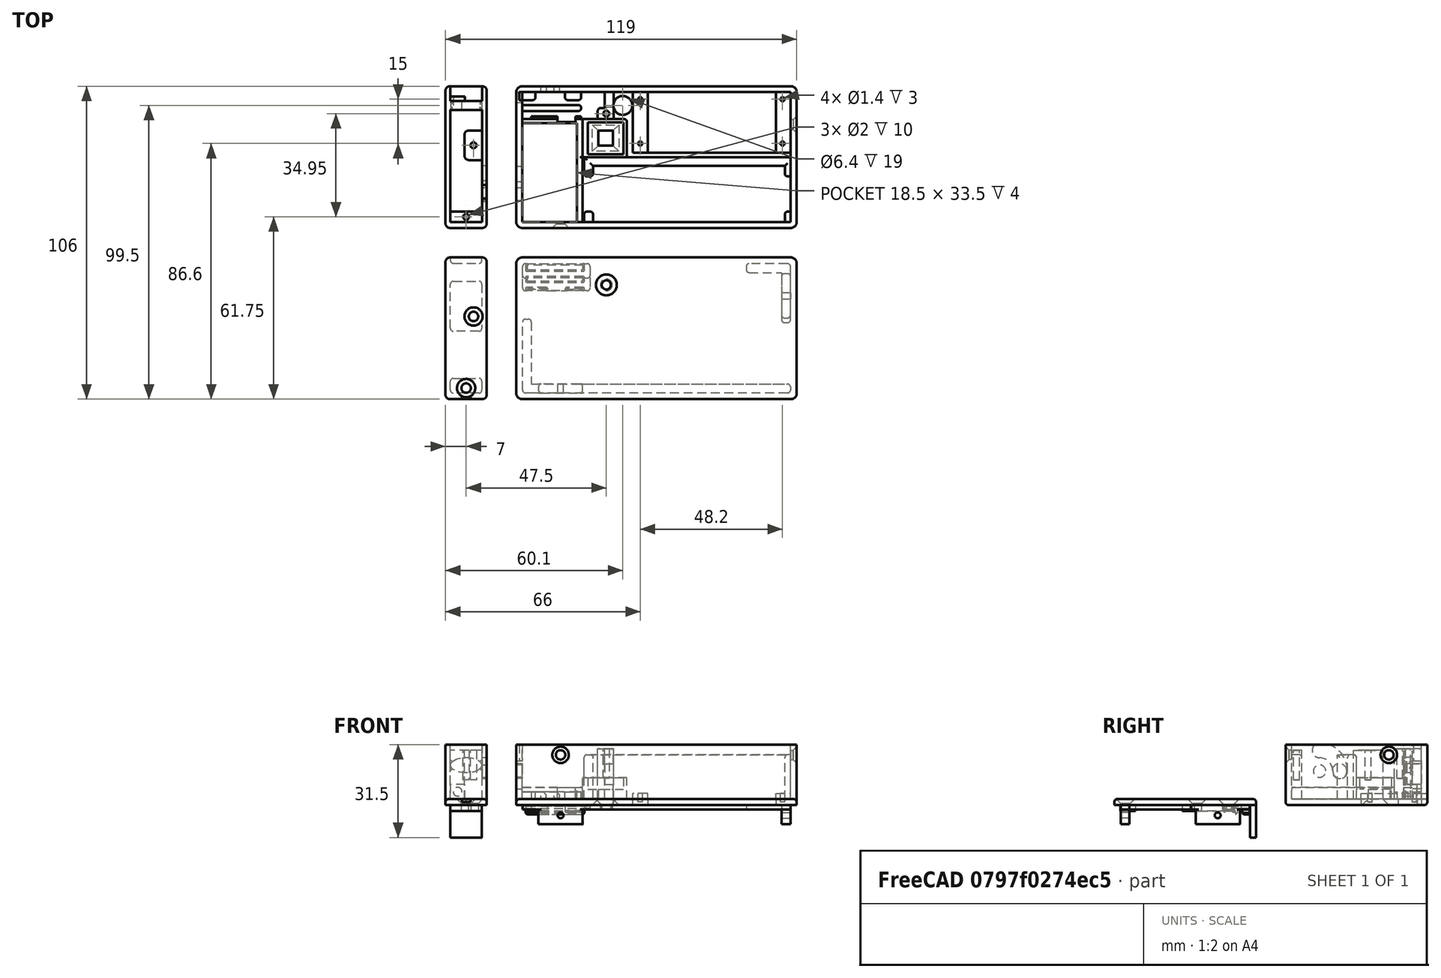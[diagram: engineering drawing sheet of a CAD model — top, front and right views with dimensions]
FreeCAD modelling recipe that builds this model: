
FCSTD DOCUMENT  (FreeCAD 0.19R23756 (Git))
Label: uv_case
License: All rights reserved
LicenseURL: http://en.wikipedia.org/wiki/All_rights_reserved
objects: Sketcher::SketchObject×52, PartDesign::Pocket×23, PartDesign::Pad×22, PartDesign::Fillet×16, PartDesign::Chamfer×7, PartDesign::Body×4, Mesh::Feature×4
note: 192 computed .brp shape members not serialized (recipe doc carries the construction recipe); baked Part::Feature solids carry a one-line shape summary decoded from their .brp

FEATURE [Sketcher::SketchObject] Sketch
  FullyConstrained = true
  MapMode = 5
  Support = -> [XY_Plane]
  sketch-geometry (4):
    g0: LineSegment StartX=0 StartY=0 StartZ=0 EndX=95 EndY=0 EndZ=0
    g1: LineSegment StartX=95 StartY=0 StartZ=0 EndX=95 EndY=48 EndZ=0
    g2: LineSegment StartX=95 StartY=48 StartZ=0 EndX=0 EndY=48 EndZ=0
    g3: LineSegment StartX=0 StartY=48 StartZ=0 EndX=0 EndY=0 EndZ=0
  constraints (11):
    c: Coincident(g0,g1)
    c: Coincident(g1,g2)
    c: Coincident(g2,g3)
    c: Coincident(g3,g0)
    c: Horizontal(g0)
    c: Horizontal(g2)
    c: Vertical(g1)
    c: Vertical(g3)
    c: Coincident(g0,g-1)
    c: DistanceX(g2,g2) = 95
    c: DistanceY(g3,g3) = 48
FEATURE [PartDesign::Pad] Pad
  Direction = (1,1,1)
  Length = 2
  Length2 = 100
  Profile = -> Sketch
  Type = 0
FEATURE [Sketcher::SketchObject] Sketch001
  ExternalGeometry = -> [Pad]
  FullyConstrained = true
  MapMode = 5
  Placement = pos=(0,0,2) rot=(0,0,1;0rad)
  Support = -> [Pad]
  sketch-geometry (8):
    g0: LineSegment StartX=0 StartY=0 StartZ=0 EndX=95 EndY=0 EndZ=0
    g1: LineSegment StartX=95 StartY=0 StartZ=0 EndX=95 EndY=48 EndZ=0
    g2: LineSegment StartX=95 StartY=48 StartZ=0 EndX=0 EndY=48 EndZ=0
    g3: LineSegment StartX=0 StartY=48 StartZ=0 EndX=0 EndY=0 EndZ=0
    g4: LineSegment StartX=2 StartY=2 StartZ=0 EndX=93 EndY=2 EndZ=0
    g5: LineSegment StartX=93 StartY=2 StartZ=0 EndX=93 EndY=46 EndZ=0
    g6: LineSegment StartX=93 StartY=46 StartZ=0 EndX=2 EndY=46 EndZ=0
    g7: LineSegment StartX=2 StartY=46 StartZ=0 EndX=2 EndY=2 EndZ=0
  constraints (22):
    c: Coincident(g0,g1)
    c: Coincident(g1,g2)
    c: Coincident(g2,g3)
    c: Coincident(g3,g0)
    c: Horizontal(g0)
    c: Horizontal(g2)
    c: Vertical(g1)
    c: Vertical(g3)
    c: Coincident(g0,g-1)
    c: Coincident(g1,g-3)
    c: Coincident(g4,g5)
    c: Coincident(g5,g6)
    c: Coincident(g6,g7)
    c: Coincident(g7,g4)
    c: Horizontal(g4)
    c: Horizontal(g6)
    c: Vertical(g5)
    c: Vertical(g7)
    c: DistanceX(g5,g1) = 2
    c: DistanceY(g5,g1) = 2
    c: DistanceX(g0,g4) = 2
    c: DistanceY(g0,g4) = 2
FEATURE [PartDesign::Pad] Pad001
  BaseFeature = -> Pad
  Direction = (1,1,1)
  Length = 18.5
  Length2 = 100
  Profile = -> Sketch001
  Type = 0
FEATURE [Sketcher::SketchObject] Sketch002
  ExternalGeometry = -> [Pad001]
  FullyConstrained = true
  MapMode = 5
  Placement = pos=(0,0,2) rot=(0,0,1;0rad)
  Support = -> [Pad001]
  sketch-geometry (4):
    g0: LineSegment StartX=44.5 StartY=46 StartZ=0 EndX=88 EndY=46 EndZ=0
    g1: LineSegment StartX=88 StartY=46 StartZ=0 EndX=88 EndY=25.5 EndZ=0
    g2: LineSegment StartX=88 StartY=25.5 StartZ=0 EndX=44.5 EndY=25.5 EndZ=0
    g3: LineSegment StartX=44.5 StartY=25.5 StartZ=0 EndX=44.5 EndY=46 EndZ=0
  constraints (12):
    c: Coincident(g0,g1)
    c: Coincident(g1,g2)
    c: Coincident(g2,g3)
    c: Coincident(g3,g0)
    c: Horizontal(g0)
    c: Horizontal(g2)
    c: Vertical(g1)
    c: Vertical(g3)
    c: Horizontal(g0,g-3)
    c: DistanceX(g0,g-3) = 5
    c: DistanceX(g2,g2) = 43.5
    c: DistanceY(g3,g3) = 20.5
FEATURE [PartDesign::Pocket] Pocket
  BaseFeature = -> Pad001
  Length = 5
  Length2 = 100
  Profile = -> Sketch002
  Type = 0
FEATURE [Sketcher::SketchObject] Sketch003
  ExternalGeometry = -> [Pocket]
  FullyConstrained = true
  MapMode = 5
  Placement = pos=(0,0,2) rot=(0,0,1;0rad)
  Support = -> [Pocket]
  sketch-geometry (8):
    g0: LineSegment StartX=39.5 StartY=25.5 StartZ=0 EndX=44.5 EndY=25.5 EndZ=0
    g1: LineSegment StartX=44.5 StartY=25.5 StartZ=0 EndX=44.5 EndY=46 EndZ=0
    g2: LineSegment StartX=44.5 StartY=46 StartZ=0 EndX=39.5 EndY=46 EndZ=0
    g3: LineSegment StartX=39.5 StartY=46 StartZ=0 EndX=39.5 EndY=25.5 EndZ=0
    g4: LineSegment StartX=88 StartY=46 StartZ=0 EndX=93 EndY=46 EndZ=0
    g5: LineSegment StartX=93 StartY=46 StartZ=0 EndX=93 EndY=25.5 EndZ=0
    g6: LineSegment StartX=93 StartY=25.5 StartZ=0 EndX=88 EndY=25.5 EndZ=0
    g7: LineSegment StartX=88 StartY=25.5 StartZ=0 EndX=88 EndY=46 EndZ=0
  constraints (20):
    c: Coincident(g0,g1)
    c: Coincident(g1,g2)
    c: Coincident(g2,g3)
    c: Coincident(g3,g0)
    c: Horizontal(g0)
    c: Horizontal(g2)
    c: Vertical(g3)
    c: Coincident(g4,g5)
    c: Coincident(g5,g6)
    c: Coincident(g6,g7)
    c: Coincident(g7,g4)
    c: Horizontal(g4)
    c: Horizontal(g6)
    c: Vertical(g5)
    c: Coincident(g1,g-4)
    c: Coincident(g0,g-4)
    c: Coincident(g6,g-3)
    c: Coincident(g4,g-3)
    c: DistanceX(g6,g6) = 5
    c: DistanceX(g0,g0) = 5
FEATURE [PartDesign::Pad] Pad002
  BaseFeature = -> Pocket
  Direction = (1,1,1)
  Length = 2
  Length2 = 100
  Profile = -> Sketch003
  Type = 0
FEATURE [Sketcher::SketchObject] Sketch004
  ExternalGeometry = -> [Pad002]
  FullyConstrained = true
  MapMode = 5
  Placement = pos=(0,0,4) rot=(0,0,1;0rad)
  Support = -> [Pad002]
  sketch-geometry (4):
    g0: Circle CenterX=90.2 CenterY=43.6 CenterZ=0 NormalX=0 NormalY=0 NormalZ=1 AngleXU=0 Radius=0.7
    g1: Circle CenterX=90.2 CenterY=28.6 CenterZ=0 NormalX=0 NormalY=0 NormalZ=1 AngleXU=0 Radius=0.7
    g2: Circle CenterX=42 CenterY=43.6 CenterZ=0 NormalX=0 NormalY=0 NormalZ=1 AngleXU=0 Radius=0.7
    g3: Circle CenterX=42 CenterY=28.6 CenterZ=0 NormalX=0 NormalY=0 NormalZ=1 AngleXU=0 Radius=0.7
  constraints (12):
    c: DistanceX(g-3,g0) = 2.2
    c: DistanceX(g2,g-4) = 2.5
    c: Vertical(g2,g3)
    c: Vertical(g0,g1)
    c: Horizontal(g1,g3)
    c: Horizontal(g2,g0)
    c: Equal(g0,g2)
    c: Equal(g2,g3)
    c: Equal(g3,g1)
    c: DistanceY(g3,g2) = 15
    c: DistanceY(g2,g-4) = 2.4
    c: Radius(g2) = 0.7
FEATURE [PartDesign::Pocket] Pocket001
  BaseFeature = -> Pad002
  Length = 3
  Length2 = 100
  Profile = -> Sketch004
  Type = 0
FEATURE [Sketcher::SketchObject] Sketch005
  ExternalGeometry = -> [Pocket001]
  FullyConstrained = true
  MapMode = 5
  Placement = pos=(0,0,2) rot=(0,0,1;0rad)
  Support = -> [Pocket001]
  sketch-geometry (20):
    g0: LineSegment StartX=2 StartY=46 StartZ=0 EndX=6.5 EndY=46 EndZ=0
    g1: LineSegment StartX=6.5 StartY=46 StartZ=0 EndX=6.5 EndY=43.3 EndZ=0
    g2: LineSegment StartX=6.5 StartY=43.3 StartZ=0 EndX=2 EndY=43.3 EndZ=0
    g3: LineSegment StartX=2 StartY=43.3 StartZ=0 EndX=2 EndY=46 EndZ=0
    g4: LineSegment StartX=16.5 StartY=46 StartZ=0 EndX=22 EndY=46 EndZ=0
    g5: LineSegment StartX=22 StartY=46 StartZ=0 EndX=22 EndY=43.3 EndZ=0
    g6: LineSegment StartX=22 StartY=43.3 StartZ=0 EndX=16.5 EndY=43.3 EndZ=0
    g7: LineSegment StartX=16.5 StartY=43.3 StartZ=0 EndX=16.5 EndY=46 EndZ=0
    g8: LineSegment StartX=2 StartY=41.6 StartZ=0 EndX=22 EndY=41.6 EndZ=0
    g9: LineSegment StartX=22 StartY=41.6 StartZ=0 EndX=22 EndY=39.6 EndZ=0
    g10: LineSegment StartX=22 StartY=39.6 StartZ=0 EndX=2 EndY=39.6 EndZ=0
    g11: LineSegment StartX=2 StartY=39.6 StartZ=0 EndX=2 EndY=41.6 EndZ=0
    g12: LineSegment StartX=2 StartY=36.85 StartZ=0 EndX=14 EndY=36.85 EndZ=0
    g13: LineSegment StartX=14 StartY=36.85 StartZ=0 EndX=14 EndY=37.85 EndZ=0
    g14: LineSegment StartX=14 StartY=37.85 StartZ=0 EndX=2 EndY=37.85 EndZ=0
    g15: LineSegment StartX=2 StartY=37.85 StartZ=0 EndX=2 EndY=36.85 EndZ=0
    g16: LineSegment StartX=20 StartY=37.85 StartZ=0 EndX=22 EndY=37.85 EndZ=0
    g17: LineSegment StartX=22 StartY=37.85 StartZ=0 EndX=22 EndY=36.85 EndZ=0
    g18: LineSegment StartX=22 StartY=36.85 StartZ=0 EndX=20 EndY=36.85 EndZ=0
    g19: LineSegment StartX=20 StartY=36.85 StartZ=0 EndX=20 EndY=37.85 EndZ=0
  constraints (59):
    c: Coincident(g0,g1)
    c: Coincident(g1,g2)
    c: Coincident(g2,g3)
    c: Coincident(g3,g0)
    c: Horizontal(g0)
    c: Horizontal(g2)
    c: Vertical(g1)
    c: Vertical(g3)
    c: Coincident(g4,g5)
    c: Coincident(g5,g6)
    c: Coincident(g6,g7)
    c: Coincident(g7,g4)
    c: Horizontal(g4)
    c: Horizontal(g6)
    c: Vertical(g5)
    c: Vertical(g7)
    c: Coincident(g8,g9)
    c: Coincident(g9,g10)
    c: Coincident(g10,g11)
    c: Coincident(g11,g8)
    c: Horizontal(g8)
    c: Vertical(g9)
    c: Vertical(g11)
    c: Coincident(g12,g13)
    c: Coincident(g13,g14)
    c: Coincident(g14,g15)
    c: Coincident(g15,g12)
    c: Horizontal(g12)
    c: Horizontal(g14)
    c: Vertical(g13)
    c: Vertical(g15)
    c: DistanceY(g3,g3) = 2.7
    c: DistanceX(g0,g0) = 4.5
    c: Coincident(g0,g-3)
    c: Horizontal(g4,g0)
    c: Horizontal(g6,g1)
    c: DistanceX(g0,g4) = 14.5
    c: DistanceX(g0,g4) = 20
    c: DistanceY(g8,g2) = 1.7
    c: DistanceX(g8,g8) = 20
    c: DistanceY(g11,g11) = 2
    c: Vertical(g8,g2)
    c: Horizontal(g10)
    c: DistanceX(g14,g14) = 12
    c: DistanceY(g15,g15) = 1
    c: Vertical(g14,g10)
    c: DistanceY(g14,g10) = 1.75
    c: Coincident(g16,g17)
    c: Coincident(g17,g18)
    c: Coincident(g18,g19)
    c: Coincident(g19,g16)
    c: Horizontal(g16)
    c: Horizontal(g18)
    c: Vertical(g17)
    c: Vertical(g19)
    c: Horizontal(g18,g12)
    c: Horizontal(g13,g16)
    c: DistanceX(g12,g18) = 18
    c: DistanceX(g12,g17) = 20
FEATURE [PartDesign::Pad] Pad003
  BaseFeature = -> Pocket001
  Direction = (1,1,1)
  Length = 2.5
  Length2 = 100
  Profile = -> Sketch005
  Type = 0
FEATURE [Sketcher::SketchObject] Sketch006
  ExternalGeometry = -> [Pad003]
  FullyConstrained = true
  MapMode = 5
  Placement = pos=(0,0,2) rot=(0,0,1;0rad)
  Support = -> [Pad003]
  sketch-geometry (7):
    g0: LineSegment StartX=30 StartY=46 StartZ=0 EndX=33 EndY=46 EndZ=0
    g1: LineSegment StartX=33 StartY=46 StartZ=0 EndX=33 EndY=36.85 EndZ=0
    g2: LineSegment StartX=33 StartY=36.85 StartZ=0 EndX=27.6 EndY=36.85 EndZ=0
    g3: LineSegment StartX=30 StartY=40.6 StartZ=0 EndX=30 EndY=46 EndZ=0
    g4: LineSegment StartX=27.6 StartY=36.85 StartZ=0 EndX=27.6 EndY=40.6 EndZ=0
    g5: LineSegment StartX=27.6 StartY=40.6 StartZ=0 EndX=30 EndY=40.6 EndZ=0
    g6: GeomPoint X=22 Y=40.6 Z=0
  constraints (19):
    c: Coincident(g0,g1)
    c: Coincident(g1,g2)
    c: Coincident(g3,g0)
    c: Horizontal(g0)
    c: Horizontal(g2)
    c: Vertical(g1)
    c: Vertical(g3)
    c: Horizontal(g0,g-3)
    c: DistanceX(g-3,g0) = 28
    c: DistanceX(g0,g0) = 3
    c: DistanceX(g-3,g2) = 25.6
    c: Horizontal(g2,g-4)
    c: Coincident(g4,g2)
    c: Vertical(g4)
    c: Coincident(g5,g4)
    c: Horizontal(g5)
    c: Coincident(g3,g5)
    c: Symmetric(g-5,g-5,g6)
    c: Horizontal(g6,g4)
FEATURE [PartDesign::Pad] Pad004
  BaseFeature = -> Pad003
  Direction = (1,1,1)
  Length = 17
  Length2 = 100
  Profile = -> Sketch006
  Type = 0
FEATURE [Sketcher::SketchObject] Sketch007
  ExternalGeometry = -> [Pad004]
  FullyConstrained = true
  MapMode = 5
  Placement = pos=(0,0,20.5) rot=(0,0,1;0rad)
  Support = -> [Pad004]
  sketch-geometry (4):
    g0: LineSegment StartX=2 StartY=46 StartZ=0 EndX=1 EndY=46 EndZ=0
    g1: LineSegment StartX=1 StartY=46 StartZ=0 EndX=1 EndY=43.3 EndZ=0
    g2: LineSegment StartX=1 StartY=43.3 StartZ=0 EndX=2 EndY=43.3 EndZ=0
    g3: LineSegment StartX=2 StartY=43.3 StartZ=0 EndX=2 EndY=46 EndZ=0
  constraints (10):
    c: Coincident(g0,g1)
    c: Coincident(g1,g2)
    c: Coincident(g2,g3)
    c: Coincident(g3,g0)
    c: Horizontal(g0)
    c: Horizontal(g2)
    c: Vertical(g1)
    c: Coincident(g0,g-3)
    c: DistanceX(g0,g0) = 1
    c: Coincident(g2,g-4)
FEATURE [PartDesign::Pocket] Pocket002
  BaseFeature = -> Pad004
  Length = 14
  Length2 = 100
  Profile = -> Sketch007
  Type = 0
FEATURE [Sketcher::SketchObject] Sketch008
  ExternalGeometry = -> [Pocket002]
  FullyConstrained = true
  MapMode = 5
  Placement = pos=(0,0,0) rot=(0.57735,-0.57735,-0.57735;2.0944rad)
  Support = -> [Pocket002]
  sketch-geometry (4):
    g0: LineSegment StartX=-46 StartY=5.5 StartZ=0 EndX=-42.5 EndY=5.5 EndZ=0
    g1: LineSegment StartX=-42.5 StartY=5.5 StartZ=0 EndX=-42.5 EndY=15 EndZ=0
    g2: LineSegment StartX=-42.5 StartY=15 StartZ=0 EndX=-46 EndY=15 EndZ=0
    g3: LineSegment StartX=-46 StartY=15 StartZ=0 EndX=-46 EndY=5.5 EndZ=0
  constraints (12):
    c: Coincident(g0,g1)
    c: Coincident(g1,g2)
    c: Coincident(g2,g3)
    c: Coincident(g3,g0)
    c: Horizontal(g0)
    c: Horizontal(g2)
    c: Vertical(g1)
    c: Vertical(g3)
    c: DistanceX(g-3,g0) = 2
    c: DistanceY(g-3,g0) = 3.5
    c: DistanceY(g-3,g2) = 13
    c: DistanceX(g2,g2) = 3.5
FEATURE [PartDesign::Pocket] Pocket003
  BaseFeature = -> Pocket002
  Length = 2
  Length2 = 100
  Profile = -> Sketch008
  Type = 0
FEATURE [Sketcher::SketchObject] Sketch009
  ExternalGeometry = -> [Pocket003]
  FullyConstrained = true
  MapMode = 5
  Placement = pos=(0,48,0) rot=(0,0.707107,0.707107;3.14159rad)
  Support = -> [Pocket003]
  sketch-geometry (2):
    g0: Circle CenterX=-9.2 CenterY=3 CenterZ=0 NormalX=0 NormalY=0 NormalZ=1 AngleXU=0 Radius=1
    g1: Circle CenterX=-13.7 CenterY=3 CenterZ=0 NormalX=0 NormalY=0 NormalZ=1 AngleXU=0 Radius=1
  constraints (6):
    c: DistanceX(g0,g-1) = 9.2
    c: DistanceX(g1,g-1) = 13.7
    c: Equal(g1,g0)
    c: Radius(g1) = 1
    c: DistanceY(g-3,g0) = 1
    c: Horizontal(g0,g1)
FEATURE [PartDesign::Pocket] Pocket004
  BaseFeature = -> Pocket003
  Length = 2
  Length2 = 100
  Profile = -> Sketch009
  Type = 0
FEATURE [Sketcher::SketchObject] Sketch010
  ExternalGeometry = -> [Pocket004]
  FullyConstrained = true
  MapMode = 5
  Placement = pos=(0,0,2) rot=(0,0,1;0rad)
  Support = -> [Pocket004]
  sketch-geometry (10):
    g0: LineSegment StartX=2 StartY=35.5 StartZ=0 EndX=20.5 EndY=35.5 EndZ=0
    g1: LineSegment StartX=20.5 StartY=35.5 StartZ=0 EndX=20.5 EndY=2 EndZ=0
    g2: LineSegment StartX=20.5 StartY=2 StartZ=0 EndX=22.5 EndY=2 EndZ=0
    g3: LineSegment StartX=22.5 StartY=2 StartZ=0 EndX=22.5 EndY=36.85 EndZ=0
    g4: LineSegment StartX=14 StartY=36.85 StartZ=0 EndX=2 EndY=36.85 EndZ=0
    g5: LineSegment StartX=2 StartY=36.85 StartZ=0 EndX=2 EndY=35.5 EndZ=0
    g6: LineSegment StartX=14 StartY=36.85 StartZ=0 EndX=14 EndY=35.85 EndZ=0
    g7: LineSegment StartX=14 StartY=35.85 StartZ=0 EndX=20 EndY=35.85 EndZ=0
    g8: LineSegment StartX=20 StartY=35.85 StartZ=0 EndX=20 EndY=36.85 EndZ=0
    g9: LineSegment StartX=20 StartY=36.85 StartZ=0 EndX=22.5 EndY=36.85 EndZ=0
  constraints (28):
    c: Horizontal(g0)
    c: Coincident(g1,g0)
    c: Vertical(g1)
    c: Coincident(g3,g2)
    c: Vertical(g3)
    c: Horizontal(g4)
    c: Coincident(g4,g5)
    c: Coincident(g1,g2)
    c: Horizontal(g2)
    c: Vertical(g5)
    c: Coincident(g0,g5)
    c: Vertical(g-3,g0)
    c: DistanceY(g-3,g0) = 33.5
    c: Horizontal(g3,g-4)
    c: DistanceX(g0,g0) = 18.5
    c: Horizontal(g1,g-3)
    c: Coincident(g4,g-4)
    c: Coincident(g6,g4)
    c: Vertical(g6)
    c: Coincident(g7,g6)
    c: Horizontal(g7)
    c: Coincident(g8,g7)
    c: Vertical(g8)
    c: Coincident(g9,g3)
    c: DistanceX(g0,g3) = 2
    c: DistanceY(g6,g4) = 1
    c: Coincident(g8,g9)
    c: Coincident(g8,g-5)
FEATURE [PartDesign::Pad] Pad005
  BaseFeature = -> Pocket004
  Direction = (1,1,1)
  Length = 4
  Length2 = 100
  Profile = -> Sketch010
  Type = 0
FEATURE [Sketcher::SketchObject] Sketch011
  ExternalGeometry = -> [Pad005]
  FullyConstrained = true
  MapMode = 5
  Placement = pos=(0,0,2) rot=(0,0,1;0rad)
  Support = -> [Pad005]
  sketch-geometry (20):
    g0: LineSegment StartX=23 StartY=24 StartZ=0 EndX=93 EndY=24 EndZ=0
    g1: LineSegment StartX=93 StartY=24 StartZ=0 EndX=93 EndY=21 EndZ=0
    g2: LineSegment StartX=93 StartY=21 StartZ=0 EndX=23 EndY=21 EndZ=0
    g3: LineSegment StartX=23 StartY=21 StartZ=0 EndX=23 EndY=24 EndZ=0
    g4: LineSegment StartX=91 StartY=5.5 StartZ=0 EndX=93 EndY=5.5 EndZ=0
    g5: LineSegment StartX=93 StartY=5.5 StartZ=0 EndX=93 EndY=2 EndZ=0
    g6: LineSegment StartX=93 StartY=2 StartZ=0 EndX=91 EndY=2 EndZ=0
    g7: LineSegment StartX=91 StartY=2 StartZ=0 EndX=91 EndY=5.5 EndZ=0
    g8: LineSegment StartX=93 StartY=21 StartZ=0 EndX=91 EndY=21 EndZ=0
    g9: LineSegment StartX=91 StartY=21 StartZ=0 EndX=91 EndY=17.5 EndZ=0
    g10: LineSegment StartX=91 StartY=17.5 StartZ=0 EndX=93 EndY=17.5 EndZ=0
    g11: LineSegment StartX=93 StartY=17.5 StartZ=0 EndX=93 EndY=21 EndZ=0
    g12: LineSegment StartX=23 StartY=21 StartZ=0 EndX=26 EndY=21 EndZ=0
    g13: LineSegment StartX=26 StartY=21 StartZ=0 EndX=26 EndY=17.5 EndZ=0
    g14: LineSegment StartX=26 StartY=17.5 StartZ=0 EndX=23 EndY=17.5 EndZ=0
    g15: LineSegment StartX=23 StartY=17.5 StartZ=0 EndX=23 EndY=21 EndZ=0
    g16: LineSegment StartX=23 StartY=2 StartZ=0 EndX=26 EndY=2 EndZ=0
    g17: LineSegment StartX=26 StartY=2 StartZ=0 EndX=26 EndY=5.5 EndZ=0
    g18: LineSegment StartX=26 StartY=5.5 StartZ=0 EndX=23 EndY=5.5 EndZ=0
    g19: LineSegment StartX=23 StartY=5.5 StartZ=0 EndX=23 EndY=2 EndZ=0
  constraints (57):
    c: Coincident(g0,g1)
    c: Coincident(g1,g2)
    c: Coincident(g2,g3)
    c: Coincident(g3,g0)
    c: Horizontal(g0)
    c: Horizontal(g2)
    c: Vertical(g1)
    c: Vertical(g3)
    c: Vertical(g1,g-3)
    c: DistanceY(g-3,g1) = 19
    c: DistanceY(g3,g3) = 3
    c: Coincident(g4,g5)
    c: Coincident(g5,g6)
    c: Coincident(g6,g7)
    c: Coincident(g7,g4)
    c: Horizontal(g4)
    c: Horizontal(g6)
    c: Vertical(g5)
    c: Vertical(g7)
    c: Coincident(g5,g-3)
    c: Coincident(g8,g9)
    c: Coincident(g9,g10)
    c: Coincident(g10,g11)
    c: Coincident(g11,g8)
    c: Horizontal(g8)
    c: Horizontal(g10)
    c: Vertical(g9)
    c: Vertical(g11)
    c: Coincident(g8,g1)
    c: Coincident(g12,g13)
    c: Coincident(g13,g14)
    c: Coincident(g14,g15)
    c: Coincident(g15,g12)
    c: Horizontal(g12)
    c: Horizontal(g14)
    c: Vertical(g13)
    c: Vertical(g15)
    c: Coincident(g12,g2)
    c: Coincident(g16,g17)
    c: Coincident(g17,g18)
    c: Coincident(g18,g19)
    c: Coincident(g19,g16)
    c: Horizontal(g16)
    c: Horizontal(g18)
    c: Vertical(g17)
    c: Vertical(g19)
    c: PointOnObject(g16,g-3)
    c: Horizontal(g17,g4)
    c: Horizontal(g13,g9)
    c: Vertical(g14,g18)
    c: DistanceX(g14,g14) = 3
    c: Vertical(g17,g13)
    c: DistanceX(g12,g8) = 65
    c: DistanceX(g10,g10) = 2
    c: Vertical(g4,g9)
    c: Equal(g13,g17)
    c: DistanceY(g17,g17) = 3.5
FEATURE [PartDesign::Pad] Pad006
  BaseFeature = -> Pad005
  Direction = (1,1,1)
  Length = 15
  Length2 = 100
  Profile = -> Sketch011
  Type = 0
FEATURE [Sketcher::SketchObject] Sketch012
  ExternalGeometry = -> [Pad006]
  FullyConstrained = true
  MapMode = 5
  Placement = pos=(0,0,2) rot=(0,0,1;0rad)
  Support = -> [Pad006]
  sketch-geometry (4):
    g0: LineSegment StartX=22.5 StartY=36.85 StartZ=0 EndX=37.5 EndY=36.85 EndZ=0
    g1: LineSegment StartX=37.5 StartY=36.85 StartZ=0 EndX=37.5 EndY=24 EndZ=0
    g2: LineSegment StartX=37.5 StartY=24 StartZ=0 EndX=22.5 EndY=24 EndZ=0
    g3: LineSegment StartX=22.5 StartY=24 StartZ=0 EndX=22.5 EndY=36.85 EndZ=0
  constraints (11):
    c: Coincident(g0,g1)
    c: Coincident(g1,g2)
    c: Coincident(g2,g3)
    c: Coincident(g3,g0)
    c: Horizontal(g0)
    c: Horizontal(g2)
    c: Vertical(g1)
    c: Vertical(g3)
    c: DistanceX(g0,g0) = 15
    c: Coincident(g0,g-5)
    c: Horizontal(g3,g-4)
FEATURE [PartDesign::Pad] Pad007
  BaseFeature = -> Pad006
  Direction = (1,1,1)
  Length = 7.3
  Length2 = 100
  Profile = -> Sketch012
  Type = 0
FEATURE [Sketcher::SketchObject] Sketch013
  ExternalGeometry = -> [Pad007]
  FullyConstrained = true
  MapMode = 5
  Placement = pos=(0,0,9.3) rot=(0,0,1;0rad)
  Support = -> [Pad007]
  sketch-geometry (8):
    g0: LineSegment StartX=24.25 StartY=35.825 StartZ=0 EndX=36.25 EndY=35.825 EndZ=0
    g1: LineSegment StartX=36.25 StartY=35.825 StartZ=0 EndX=36.25 EndY=25.025 EndZ=0
    g2: LineSegment StartX=36.25 StartY=25.025 StartZ=0 EndX=24.25 EndY=25.025 EndZ=0
    g3: LineSegment StartX=24.25 StartY=25.025 StartZ=0 EndX=24.25 EndY=35.825 EndZ=0
    g4: GeomPoint X=37.5 Y=30.425 Z=0
    g5: GeomPoint X=30.25 Y=30.425 Z=0
    g6: GeomPoint X=30.25 Y=35.825 Z=0
    g7: GeomPoint X=36.25 Y=30.425 Z=0
  constraints (16):
    c: Coincident(g0,g1)
    c: Coincident(g1,g2)
    c: Coincident(g2,g3)
    c: Coincident(g3,g0)
    c: Horizontal(g0)
    c: Horizontal(g2)
    c: Vertical(g1)
    c: Vertical(g3)
    c: Symmetric(g-4,g-5,g5)
    c: Symmetric(g-5,g-5,g4)
    c: Symmetric(g0,g0,g6)
    c: Symmetric(g0,g1,g7)
    c: Vertical(g6,g5)
    c: Horizontal(g7,g4)
    c: DistanceY(g3,g3) = 10.8
    c: DistanceX(g0,g0) = 12
FEATURE [PartDesign::Pocket] Pocket005
  BaseFeature = -> Pad007
  Length = 4
  Length2 = 100
  Profile = -> Sketch013
  Type = 0
FEATURE [Sketcher::SketchObject] Sketch014
  ExternalGeometry = -> [Pocket005]
  FullyConstrained = true
  MapMode = 5
  Placement = pos=(0,0,5.3) rot=(0,0,1;0rad)
  Support = -> [Pocket005]
  sketch-geometry (8):
    g0: GeomPoint X=24.25 Y=30.425 Z=0
    g1: GeomPoint X=30.25 Y=35.825 Z=0
    g2: LineSegment StartX=27.75 StartY=32.925 StartZ=0 EndX=32.75 EndY=32.925 EndZ=0
    g3: LineSegment StartX=32.75 StartY=32.925 StartZ=0 EndX=32.75 EndY=27.925 EndZ=0
    g4: LineSegment StartX=32.75 StartY=27.925 StartZ=0 EndX=27.75 EndY=27.925 EndZ=0
    g5: LineSegment StartX=27.75 StartY=27.925 StartZ=0 EndX=27.75 EndY=32.925 EndZ=0
    g6: GeomPoint X=30.25 Y=32.925 Z=0
    g7: GeomPoint X=27.75 Y=30.425 Z=0
  constraints (16):
    c: Symmetric(g-3,g-3,g0)
    c: Symmetric(g-3,g-4,g1)
    c: Coincident(g2,g3)
    c: Coincident(g3,g4)
    c: Coincident(g4,g5)
    c: Coincident(g5,g2)
    c: Horizontal(g2)
    c: Horizontal(g4)
    c: Vertical(g3)
    c: Vertical(g5)
    c: Symmetric(g2,g2,g6)
    c: Symmetric(g2,g4,g7)
    c: Horizontal(g7,g0)
    c: Vertical(g1,g6)
    c: DistanceX(g2,g2) = 5
    c: DistanceY(g3,g3) = 5
FEATURE [PartDesign::Pocket] Pocket006
  BaseFeature = -> Pocket005
  Length = 6
  Length2 = 100
  Profile = -> Sketch014
  Type = 0
FEATURE [Sketcher::SketchObject] Sketch015
  ExternalGeometry = -> [Pocket006]
  FullyConstrained = true
  MapMode = 5
  Placement = pos=(0,0,2) rot=(0,0,1;0rad)
  Support = -> [Pocket006]
  sketch-geometry (1):
    g0: Circle CenterX=36.1 CenterY=41.5 CenterZ=0 NormalX=0 NormalY=0 NormalZ=1 AngleXU=0 Radius=3.2
  constraints (3):
    c: Radius(g0) = 3.2
    c: DistanceX(g-3,g0) = 3.1
    c: DistanceY(g0,g-3) = 4.5
FEATURE [PartDesign::Pocket] Pocket007
  BaseFeature = -> Pocket006
  Length = 5
  Length2 = 100
  Profile = -> Sketch015
  Type = 4
FEATURE [Sketcher::SketchObject] Sketch016
  ExternalGeometry = -> [Pocket007]
  FullyConstrained = true
  MapMode = 5
  Placement = pos=(0,0,19) rot=(0,0,1;0rad)
  Support = -> [Pocket007]
  constraints (1):
    c: DistanceY(g-4,g-3) = 3.75
FEATURE [Sketcher::SketchObject] Sketch017
  ExternalGeometry = -> [Pocket007]
  FullyConstrained = true
  MapMode = 5
  Placement = pos=(0,0,19) rot=(0,0,1;0rad)
  Support = -> [Pocket007]
  sketch-geometry (1):
    g0: Circle CenterX=30.5 CenterY=38.7 CenterZ=0 NormalX=0 NormalY=0 NormalZ=1 AngleXU=0 Radius=1
  constraints (3):
    c: Radius(g0) = 1
    c: DistanceX(g-4,g0) = 30.5
    c: DistanceY(g0,g-4) = 9.3
FEATURE [PartDesign::Pocket] Pocket008
  BaseFeature = -> Pocket007
  Length = 10
  Length2 = 100
  Profile = -> Sketch017
  Type = 0
FEATURE [Sketcher::SketchObject] Sketch018
  FullyConstrained = true
  MapMode = 5
  Placement = pos=(0,0,0) rot=(1,0,0;1.5708rad)
  Support = -> [Pocket008]
  sketch-geometry (1):
    g0: Circle CenterX=15 CenterY=17 CenterZ=0 NormalX=0 NormalY=0 NormalZ=1 AngleXU=0 Radius=1.6
  constraints (3):
    c: Radius(g0) = 1.6
    c: DistanceX(g-1,g0) = 15
    c: DistanceY(g-1,g0) = 17
FEATURE [PartDesign::Pocket] Pocket009
  BaseFeature = -> Pocket008
  Length = 5
  Length2 = 100
  Profile = -> Sketch018
  Type = 0
FEATURE [Sketcher::SketchObject] Sketch019
  FullyConstrained = true
  MapMode = 5
  Placement = pos=(95,0,0) rot=(0.57735,0.57735,0.57735;2.0944rad)
  Support = -> [Pocket009]
  sketch-geometry (1):
    g0: Circle CenterX=35 CenterY=17 CenterZ=0 NormalX=0 NormalY=0 NormalZ=1 AngleXU=0 Radius=1.6
  constraints (3):
    c: DistanceY(g-1,g0) = 17
    c: Radius(g0) = 1.6
    c: DistanceX(g-1,g0) = 35
FEATURE [PartDesign::Pocket] Pocket010
  BaseFeature = -> Pocket009
  Length = 5
  Length2 = 100
  Profile = -> Sketch019
  Type = 0
FEATURE [Sketcher::SketchObject] Sketch020
  FullyConstrained = true
  MapMode = 5
  Support = -> [XY_Plane001]
  sketch-geometry (4):
    g0: LineSegment StartX=-10 StartY=0 StartZ=0 EndX=-24 EndY=0 EndZ=0
    g1: LineSegment StartX=-24 StartY=0 StartZ=0 EndX=-24 EndY=48 EndZ=0
    g2: LineSegment StartX=-24 StartY=48 StartZ=0 EndX=-10 EndY=48 EndZ=0
    g3: LineSegment StartX=-10 StartY=48 StartZ=0 EndX=-10 EndY=0 EndZ=0
  constraints (12):
    c: Coincident(g0,g1)
    c: Coincident(g1,g2)
    c: Coincident(g2,g3)
    c: Coincident(g3,g0)
    c: Horizontal(g0)
    c: Horizontal(g2)
    c: Vertical(g1)
    c: Vertical(g3)
    c: PointOnObject(g0,g-1)
    c: DistanceY(g3,g3) = 48
    c: DistanceX(g2,g2) = 14
    c: DistanceX(g0,g-1) = 10
FEATURE [PartDesign::Pad] Pad008
  Direction = (1,1,1)
  Length = 2
  Length2 = 100
  Profile = -> Sketch020
  Type = 0
FEATURE [Sketcher::SketchObject] Sketch021
  ExternalGeometry = -> [Pad008]
  FullyConstrained = true
  MapMode = 5
  Placement = pos=(0,0,2) rot=(0,0,1;0rad)
  Support = -> [Pad008]
  sketch-geometry (12):
    g0: LineSegment StartX=-24 StartY=48 StartZ=0 EndX=-22.4 EndY=48 EndZ=0
    g1: LineSegment StartX=-22.4 StartY=48 StartZ=0 EndX=-22.4 EndY=43 EndZ=0
    g2: LineSegment StartX=-22.4 StartY=43 StartZ=0 EndX=-11.6 EndY=43 EndZ=0
    g3: LineSegment StartX=-11.6 StartY=43 StartZ=0 EndX=-11.6 EndY=48 EndZ=0
    g4: LineSegment StartX=-11.6 StartY=48 StartZ=0 EndX=-10 EndY=48 EndZ=0
    g5: LineSegment StartX=-10 StartY=48 StartZ=0 EndX=-10 EndY=0 EndZ=0
    g6: LineSegment StartX=-10 StartY=0 StartZ=0 EndX=-24 EndY=0 EndZ=0
    g7: LineSegment StartX=-24 StartY=0 StartZ=0 EndX=-24 EndY=48 EndZ=0
    g8: LineSegment StartX=-22.4 StartY=40 StartZ=0 EndX=-11.6 EndY=40 EndZ=0
    g9: LineSegment StartX=-11.6 StartY=40 StartZ=0 EndX=-11.6 EndY=2 EndZ=0
    g10: LineSegment StartX=-11.6 StartY=2 StartZ=0 EndX=-22.4 EndY=2 EndZ=0
    g11: LineSegment StartX=-22.4 StartY=2 StartZ=0 EndX=-22.4 EndY=40 EndZ=0
  constraints (33):
    c: Horizontal(g0)
    c: Coincident(g0,g1)
    c: Vertical(g1)
    c: Coincident(g1,g2)
    c: Horizontal(g2)
    c: Coincident(g2,g3)
    c: Vertical(g3)
    c: Coincident(g3,g4)
    c: Coincident(g4,g5)
    c: Coincident(g5,g6)
    c: Coincident(g6,g7)
    c: Coincident(g7,g0)
    c: Horizontal(g8)
    c: Coincident(g8,g9)
    c: Vertical(g9)
    c: Coincident(g9,g10)
    c: Coincident(g10,g11)
    c: Coincident(g11,g8)
    c: Vertical(g11)
    c: Coincident(g5,g-4)
    c: Coincident(g6,g-5)
    c: Coincident(g0,g-5)
    c: Coincident(g4,g-4)
    c: Horizontal(g4)
    c: Vertical(g3,g8)
    c: Vertical(g2,g8)
    c: Equal(g0,g4)
    c: DistanceX(g0,g0) = 1.6
    c: DistanceX(g2,g2) = 10.8
    c: DistanceY(g8,g2) = 3
    c: DistanceY(g1,g0) = 5
    c: DistanceY(g6,g10) = 2
    c: Horizontal(g10)
FEATURE [PartDesign::Pad] Pad009
  BaseFeature = -> Pad008
  Direction = (1,1,1)
  Length = 18.5
  Length2 = 100
  Profile = -> Sketch021
  Type = 0
FEATURE [Sketcher::SketchObject] Sketch022
  ExternalGeometry = -> [Pad009]
  FullyConstrained = true
  MapMode = 5
  Placement = pos=(0,43,0) rot=(0,0.707107,0.707107;3.14159rad)
  Support = -> [Pad009]
  sketch-geometry (4):
    g0: LineSegment StartX=22.4 StartY=2 StartZ=0 EndX=17.4 EndY=2 EndZ=0
    g1: LineSegment StartX=17.4 StartY=2 StartZ=0 EndX=17.4 EndY=7 EndZ=0
    g2: LineSegment StartX=17.4 StartY=7 StartZ=0 EndX=22.4 EndY=7 EndZ=0
    g3: LineSegment StartX=22.4 StartY=7 StartZ=0 EndX=22.4 EndY=2 EndZ=0
  constraints (11):
    c: Coincident(g0,g1)
    c: Coincident(g1,g2)
    c: Coincident(g2,g3)
    c: Coincident(g3,g0)
    c: Horizontal(g0)
    c: Horizontal(g2)
    c: Vertical(g1)
    c: Vertical(g3)
    c: Coincident(g0,g-4)
    c: DistanceX(g2,g2) = 5
    c: DistanceY(g1,g1) = 5
FEATURE [PartDesign::Pad] Pad010
  BaseFeature = -> Pad009
  Direction = (1,1,1)
  Length = 1.5
  Length2 = 100
  Profile = -> Sketch022
  Type = 0
FEATURE [Sketcher::SketchObject] Sketch023
  ExternalGeometry = -> [Pad010]
  FullyConstrained = true
  MapMode = 5
  Placement = pos=(0,44.5,0) rot=(0,0.707107,0.707107;3.14159rad)
  Support = -> [Pad010]
  sketch-geometry (1):
    g0: Circle CenterX=19.9 CenterY=4.5 CenterZ=0 NormalX=0 NormalY=0 NormalZ=1 AngleXU=0 Radius=1.5
  constraints (3):
    c: DistanceX(g-3,g0) = 2.5
    c: DistanceY(g0,g-3) = 2.5
    c: Radius(g0) = 1.5
FEATURE [PartDesign::Pocket] Pocket011
  BaseFeature = -> Pad010
  Length = 10
  Length2 = 100
  Profile = -> Sketch023
  Type = 0
FEATURE [Sketcher::SketchObject] Sketch024
  ExternalGeometry = -> [Pocket011]
  FullyConstrained = true
  MapMode = 5
  Placement = pos=(0,43,0) rot=(0,0.707107,0.707107;3.14159rad)
  Support = -> [Pocket011]
  sketch-geometry (6):
    g0: Ellipse CenterX=17 CenterY=13.5 CenterZ=0 NormalX=0 NormalY=0 NormalZ=1 MajorRadius=5.25 MinorRadius=2.62783 AngleXU=0
    g1: LineSegment StartX=22.25 StartY=13.5 StartZ=0 EndX=11.75 EndY=13.5 EndZ=0
    g2: LineSegment StartX=17 StartY=16.1278 StartZ=0 EndX=17 EndY=10.8722 EndZ=0
    g3: GeomPoint X=21.545 Y=13.5 Z=0
    g4: GeomPoint X=12.455 Y=13.5 Z=0
    g5: GeomPoint X=17 Y=20.5 Z=0
  constraints (7):
    c: InternalAlignment(g1-g4 -> g0) x4
    c: Symmetric(g-3,g-4,g5)
    c: Vertical(g5,g0)
    c: DistanceX(g1,g1) = 10.5
    c: DistanceY(g-5,g0) = 11.5
    c: Horizontal(g1)
    c: DistanceX(g4,g3) = 9.09
FEATURE [PartDesign::Pocket] Pocket012
  BaseFeature = -> Pocket011
  Length = 5
  Length2 = 100
  Profile = -> Sketch024
  Type = 0
FEATURE [Sketcher::SketchObject] Sketch025
  ExternalGeometry = -> [Pocket012]
  FullyConstrained = true
  MapMode = 5
  Placement = pos=(-10,0,0) rot=(0.57735,0.57735,0.57735;2.0944rad)
  Support = -> [Pocket012]
  sketch-geometry (5):
    g0: Circle CenterX=11.5 CenterY=11.5 CenterZ=0 NormalX=0 NormalY=0 NormalZ=1 AngleXU=0 Radius=2.1
    g1: ArcOfCircle CenterX=11.5 CenterY=11.5 CenterZ=0 NormalX=0 NormalY=0 NormalZ=1 AngleXU=0 Radius=4.5 StartAngle=0 EndAngle=1.5708
    g2: ArcOfCircle CenterX=11.5 CenterY=11.5 CenterZ=0 NormalX=0 NormalY=0 NormalZ=1 AngleXU=0 Radius=9.5 StartAngle=0 EndAngle=1.5708
    g3: ArcOfCircle CenterX=11.5 CenterY=18.5 CenterZ=0 NormalX=0 NormalY=0 NormalZ=1 AngleXU=0 Radius=2.5 StartAngle=1.5708 EndAngle=4.71239
    g4: ArcOfCircle CenterX=18.5 CenterY=11.5 CenterZ=0 NormalX=0 NormalY=0 NormalZ=1 AngleXU=0 Radius=2.5 StartAngle=3.14159 EndAngle=6.28319
  constraints (17):
    c: DistanceY(g-3,g0) = 9.5
    c: DistanceX(g-3,g0) = 11.5
    c: Radius(g0) = 2.1
    c: Coincident(g1,g0)
    c: Coincident(g2,g0)
    c: Horizontal(g1,g2)
    c: Vertical(g1,g2)
    c: Vertical(g0,g1)
    c: Horizontal(g1,g0)
    c: Coincident(g3,g1)
    c: Coincident(g3,g2)
    c: Coincident(g4,g1)
    c: Coincident(g4,g2)
    c: Symmetric(g1,g2,g4)
    c: Symmetric(g1,g2,g3)
    c: Radius(g4) = 2.5
    c: DistanceY(g0,g1) = 4.5
FEATURE [PartDesign::Pocket] Pocket013
  BaseFeature = -> Pocket012
  Length = 5
  Length2 = 100
  Profile = -> Sketch025
  Type = 0
FEATURE [Sketcher::SketchObject] Sketch026
  ExternalGeometry = -> [Pocket010]
  FullyConstrained = true
  MapMode = 5
  Placement = pos=(0,0,0) rot=(0.57735,-0.57735,-0.57735;2.0944rad)
  Support = -> [Pocket010]
  sketch-geometry (2):
    g0: Circle CenterX=-11.5 CenterY=11.5 CenterZ=0 NormalX=0 NormalY=0 NormalZ=1 AngleXU=0 Radius=2.1
    g1: Circle CenterX=-18.25 CenterY=11.5 CenterZ=0 NormalX=0 NormalY=0 NormalZ=1 AngleXU=0 Radius=2.5
  constraints (6):
    c: DistanceY(g-3,g0) = 9.5
    c: DistanceX(g0,g-3) = 11.5
    c: DistanceX(g1,g0) = 6.75
    c: Radius(g0) = 2.1
    c: Radius(g1) = 2.5
    c: Horizontal(g0,g1)
FEATURE [PartDesign::Pocket] Pocket014
  BaseFeature = -> Pocket010
  Length = 5
  Length2 = 100
  Profile = -> Sketch026
  Type = 0
FEATURE [Sketcher::SketchObject] Sketch027
  FullyConstrained = true
  MapMode = 5
  Support = -> [XY_Plane002]
  sketch-geometry (4):
    g0: LineSegment StartX=0 StartY=-10 StartZ=0 EndX=95 EndY=-10 EndZ=0
    g1: LineSegment StartX=95 StartY=-10 StartZ=0 EndX=95 EndY=-58 EndZ=0
    g2: LineSegment StartX=95 StartY=-58 StartZ=0 EndX=0 EndY=-58 EndZ=0
    g3: LineSegment StartX=0 StartY=-58 StartZ=0 EndX=0 EndY=-10 EndZ=0
  constraints (12):
    c: Coincident(g0,g1)
    c: Coincident(g1,g2)
    c: Coincident(g2,g3)
    c: Coincident(g3,g0)
    c: Horizontal(g0)
    c: Horizontal(g2)
    c: Vertical(g1)
    c: Vertical(g3)
    c: PointOnObject(g0,g-2)
    c: DistanceX(g0,g0) = 95
    c: DistanceY(g1,g1) = 48
    c: DistanceY(g0,g-1) = 10
FEATURE [PartDesign::Pad] Pad011
  Direction = (1,1,1)
  Length = 2
  Length2 = 100
  Profile = -> Sketch027
  Type = 0
FEATURE [Sketcher::SketchObject] Sketch028
  ExternalGeometry = -> [Pad011]
  FullyConstrained = true
  MapMode = 5
  Placement = pos=(0,0,0) rot=(1,0,0;3.14159rad)
  Support = -> [Pad011]
  sketch-geometry (13):
    g0: Circle CenterX=30.5 CenterY=19.3 CenterZ=0 NormalX=0 NormalY=0 NormalZ=1 AngleXU=0 Radius=2
    g1: LineSegment StartX=2.1 StartY=30.9 StartZ=0 EndX=5.1 EndY=30.9 EndZ=0
    g2: LineSegment StartX=5.1 StartY=30.9 StartZ=0 EndX=5.1 EndY=52.9 EndZ=0
    g3: LineSegment StartX=5.1 StartY=52.9 StartZ=0 EndX=92.9 EndY=52.9 EndZ=0
    g4: LineSegment StartX=92.9 StartY=52.9 StartZ=0 EndX=92.9 EndY=55.9 EndZ=0
    g5: LineSegment StartX=92.9 StartY=55.9 StartZ=0 EndX=2.1 EndY=55.9 EndZ=0
    g6: LineSegment StartX=2.1 StartY=55.9 StartZ=0 EndX=2.1 EndY=30.9 EndZ=0
    g7: LineSegment StartX=89.9 StartY=32.1 StartZ=0 EndX=92.9 EndY=32.1 EndZ=0
    g8: LineSegment StartX=92.9 StartY=32.1 StartZ=0 EndX=92.9 EndY=12.1 EndZ=0
    g9: LineSegment StartX=92.9 StartY=12.1 StartZ=0 EndX=77.9 EndY=12.1 EndZ=0
    g10: LineSegment StartX=77.9 StartY=12.1 StartZ=0 EndX=77.9 EndY=15.1 EndZ=0
    g11: LineSegment StartX=77.9 StartY=15.1 StartZ=0 EndX=89.9 EndY=15.1 EndZ=0
    g12: LineSegment StartX=89.9 StartY=15.1 StartZ=0 EndX=89.9 EndY=32.1 EndZ=0
  constraints (39):
    c: DistanceY(g-3,g0) = 9.3
    c: DistanceX(g-3,g0) = 30.5
    c: Radius(g0) = 2
    c: Horizontal(g1)
    c: Coincident(g1,g2)
    c: Vertical(g2)
    c: Coincident(g2,g3)
    c: Horizontal(g3)
    c: Coincident(g3,g4)
    c: Coincident(g4,g5)
    c: Horizontal(g5)
    c: Coincident(g5,g6)
    c: Coincident(g6,g1)
    c: Vertical(g6)
    c: Vertical(g4)
    c: DistanceX(g-3,g1) = 2.1
    c: DistanceY(g5,g-4) = 2.1
    c: DistanceX(g1,g1) = 3
    c: Equal(g1,g4)
    c: DistanceX(g4,g-4) = 2.1
    c: DistanceY(g1,g5) = 25
    c: Horizontal(g7)
    c: Coincident(g7,g8)
    c: Vertical(g8)
    c: Coincident(g8,g9)
    c: Horizontal(g9)
    c: Coincident(g9,g10)
    c: Coincident(g10,g11)
    c: Horizontal(g11)
    c: Coincident(g11,g12)
    c: Coincident(g12,g7)
    c: Vertical(g12)
    c: Vertical(g10)
    c: DistanceX(g8,g-4) = 2.1
    c: DistanceY(g-4,g8) = 2.1
    c: DistanceX(g7,g7) = 3
    c: DistanceY(g10,g10) = 3
    c: DistanceY(g8,g8) = 20
    c: DistanceX(g9,g9) = 15
FEATURE [Sketcher::SketchObject] Sketch029
  ExternalGeometry = -> [Pocket014]
  FullyConstrained = true
  MapMode = 5
  Placement = pos=(0,46,0) rot=(1,0,0;1.5708rad)
  Support = -> [Pocket014]
  constraints (1):
    c: DistanceY(g-4,g-3) = 1.5
FEATURE [Sketcher::SketchObject] Sketch030
  ExternalGeometry = -> [Pocket014]
  FullyConstrained = true
  MapMode = 5
  Placement = pos=(0,0,2) rot=(0,0,1;0rad)
  Support = -> [Pocket014]
  constraints (8):
    c: DistanceX(g-4,g-5) = 30.5
    c: DistanceY(g-5,g-4) = 9.3
    c: DistanceY(g-10,g-10) = 3.2
    c: DistanceX(g-4,g-10) = 0
    c: DistanceY(g-10,g-4) = 11.4
    c: DistanceX(g-1,g-9) = 13.4
    c: DistanceY(g-6,g-4) = 6.4
    c: DistanceY(g-8,g-4) = 11.15
FEATURE [Sketcher::SketchObject] Sketch031
  ExternalGeometry = -> [Pocket014]
  FullyConstrained = true
  MapMode = 5
  Placement = pos=(0,0,0) rot=(1,0,0;1.5708rad)
  Support = -> [Pocket014]
  constraints (1):
    c: DistanceY(g-3,g-4) = 3.5
FEATURE [PartDesign::Pad] Pad012
  BaseFeature = -> Pad011
  Direction = (1,1,1)
  Length = 1.5
  Length2 = 100
  Profile = -> Sketch028
  Type = 0
FEATURE [Sketcher::SketchObject] Sketch032
  ExternalGeometry = -> [Pad012]
  FullyConstrained = true
  MapMode = 5
  Placement = pos=(0,0,0) rot=(1,0,0;3.14159rad)
  Support = -> [Pad012]
  sketch-geometry (4):
    g0: LineSegment StartX=2.1 StartY=12.1 StartZ=0 EndX=25 EndY=12.1 EndZ=0
    g1: LineSegment StartX=25 StartY=12.1 StartZ=0 EndX=25 EndY=17 EndZ=0
    g2: LineSegment StartX=25 StartY=17 StartZ=0 EndX=2.1 EndY=17 EndZ=0
    g3: LineSegment StartX=2.1 StartY=17 StartZ=0 EndX=2.1 EndY=12.1 EndZ=0
  constraints (12):
    c: Coincident(g0,g1)
    c: Coincident(g1,g2)
    c: Coincident(g2,g3)
    c: Coincident(g3,g0)
    c: Horizontal(g0)
    c: Horizontal(g2)
    c: Vertical(g1)
    c: Vertical(g3)
    c: DistanceY(g-3,g0) = 2.1
    c: DistanceY(g-3,g2) = 7
    c: DistanceX(g-3,g0) = 25
    c: DistanceX(g-3,g0) = 2.1
FEATURE [PartDesign::Pad] Pad013
  BaseFeature = -> Pad012
  Direction = (1,1,1)
  Length = 1.2
  Length2 = 100
  Profile = -> Sketch032
  Type = 0
FEATURE [Sketcher::SketchObject] Sketch033
  ExternalGeometry = -> [Pad013]
  FullyConstrained = true
  MapMode = 5
  Placement = pos=(0,0,0) rot=(1,0,0;3.14159rad)
  Support = -> [Pad013]
  sketch-geometry (4):
    g0: LineSegment StartX=2.1 StartY=17 StartZ=0 EndX=25 EndY=17 EndZ=0
    g1: LineSegment StartX=25 StartY=17 StartZ=0 EndX=25 EndY=21.3 EndZ=0
    g2: LineSegment StartX=25 StartY=21.3 StartZ=0 EndX=2.1 EndY=21.3 EndZ=0
    g3: LineSegment StartX=2.1 StartY=21.3 StartZ=0 EndX=2.1 EndY=17 EndZ=0
  constraints (10):
    c: Coincident(g0,g1)
    c: Coincident(g1,g2)
    c: Coincident(g2,g3)
    c: Coincident(g3,g0)
    c: Horizontal(g2)
    c: Vertical(g1)
    c: Vertical(g3)
    c: Coincident(g0,g-3)
    c: Coincident(g0,g-3)
    c: DistanceY(g-4,g2) = 11.3
FEATURE [PartDesign::Pad] Pad014
  BaseFeature = -> Pad013
  Direction = (1,1,1)
  Length = 0.4
  Length2 = 100
  Profile = -> Sketch033
  Type = 0
FEATURE [Sketcher::SketchObject] Sketch034
  ExternalGeometry = -> [Pad014]
  FullyConstrained = true
  MapMode = 5
  Placement = pos=(0,0,-1.5) rot=(1,0,0;3.14159rad)
  Support = -> [Pad014]
  sketch-geometry (8):
    g0: LineSegment StartX=7.5 StartY=55.9 StartZ=0 EndX=22.5 EndY=55.9 EndZ=0
    g1: LineSegment StartX=22.5 StartY=55.9 StartZ=0 EndX=22.5 EndY=52.9 EndZ=0
    g2: LineSegment StartX=22.5 StartY=52.9 StartZ=0 EndX=7.5 EndY=52.9 EndZ=0
    g3: LineSegment StartX=7.5 StartY=52.9 StartZ=0 EndX=7.5 EndY=55.9 EndZ=0
    g4: LineSegment StartX=89.9 StartY=30.5 StartZ=0 EndX=92.9 EndY=30.5 EndZ=0
    g5: LineSegment StartX=92.9 StartY=30.5 StartZ=0 EndX=92.9 EndY=15.5 EndZ=0
    g6: LineSegment StartX=92.9 StartY=15.5 StartZ=0 EndX=89.9 EndY=15.5 EndZ=0
    g7: LineSegment StartX=89.9 StartY=15.5 StartZ=0 EndX=89.9 EndY=30.5 EndZ=0
  constraints (24):
    c: Coincident(g0,g1)
    c: Coincident(g1,g2)
    c: Coincident(g2,g3)
    c: Coincident(g3,g0)
    c: Horizontal(g0)
    c: Horizontal(g2)
    c: Vertical(g1)
    c: Vertical(g3)
    c: Coincident(g4,g5)
    c: Coincident(g5,g6)
    c: Coincident(g6,g7)
    c: Coincident(g7,g4)
    c: Horizontal(g4)
    c: Horizontal(g6)
    c: Vertical(g5)
    c: Vertical(g7)
    c: PointOnObject(g0,g-3)
    c: PointOnObject(g2,g-4)
    c: PointOnObject(g4,g-5)
    c: PointOnObject(g4,g-6)
    c: DistanceX(g0,g0) = 15
    c: DistanceX(g-7,g0) = 7.5
    c: Equal(g7,g2)
    c: DistanceY(g-7,g5) = 5.5
FEATURE [PartDesign::Pad] Pad015
  BaseFeature = -> Pad014
  Direction = (1,1,1)
  Length = 5
  Length2 = 100
  Profile = -> Sketch034
  Type = 0
FEATURE [Sketcher::SketchObject] Sketch035
  ExternalGeometry = -> [Pad015]
  FullyConstrained = true
  MapMode = 5
  Placement = pos=(92.9,0,0) rot=(0.57735,0.57735,0.57735;2.0944rad)
  Support = -> [Pad015]
  sketch-geometry (1):
    g0: Circle CenterX=-23 CenterY=-3.5 CenterZ=0 NormalX=0 NormalY=0 NormalZ=1 AngleXU=0 Radius=1
  constraints (3):
    c: DistanceY(g0,g-3) = 3.5
    c: DistanceX(g0,g-3) = 13
    c: Radius(g0) = 1
FEATURE [PartDesign::Pocket] Pocket015
  BaseFeature = -> Pad015
  Length = 5
  Length2 = 100
  Profile = -> Sketch035
  Type = 0
FEATURE [Sketcher::SketchObject] Sketch036
  ExternalGeometry = -> [Pocket015]
  FullyConstrained = true
  MapMode = 5
  Placement = pos=(0,-55.9,0) rot=(1,0,0;1.5708rad)
  Support = -> [Pocket015]
  sketch-geometry (1):
    g0: Circle CenterX=15 CenterY=-3.5 CenterZ=0 NormalX=0 NormalY=0 NormalZ=1 AngleXU=0 Radius=1
  constraints (3):
    c: Radius(g0) = 1
    c: DistanceX(g-1,g0) = 15
    c: DistanceY(g0,g-1) = 3.5
FEATURE [PartDesign::Pocket] Pocket016
  BaseFeature = -> Pocket015
  Length = 5
  Length2 = 100
  Profile = -> Sketch036
  Type = 0
FEATURE [Sketcher::SketchObject] Sketch037
  ExternalGeometry = -> [Pocket016]
  FullyConstrained = true
  MapMode = 5
  Placement = pos=(0,0,-1.5) rot=(1,0,0;3.14159rad)
  Support = -> [Pocket016]
  sketch-geometry (1):
    g0: Circle CenterX=30.5 CenterY=19.3 CenterZ=0 NormalX=0 NormalY=0 NormalZ=1 AngleXU=0 Radius=1.55
  constraints (3):
    c: Coincident(g0,g-3)
    c: Radius(g0) = 1.55
    c: Radius(g-3) = 2
FEATURE [PartDesign::Pocket] Pocket017
  BaseFeature = -> Pocket016
  Length = 7
  Length2 = 100
  Profile = -> Sketch037
  Type = 0
FEATURE [PartDesign::Fillet] Fillet
  Base = -> Pocket017 [Edge5,Edge1,Edge8,Edge2]
  BaseFeature = -> Pocket017
  Radius = 2
  SupportTransform = false
FEATURE [PartDesign::Fillet] Fillet001
  Base = -> Fillet [Edge39]
  BaseFeature = -> Fillet
  Radius = 1
  SupportTransform = false
FEATURE [PartDesign::Chamfer] Chamfer
  Angle = 45
  Base = -> Fillet001 [Edge48]
  BaseFeature = -> Fillet001
  ChamferType = 0
  FlipDirection = false
  Size = 2
  Size2 = 1
  SupportTransform = false
FEATURE [PartDesign::Fillet] Fillet002
  Base = -> Chamfer [Edge67,Edge68,Edge107,Edge111,Edge99,Edge100,Edge103,Edge105,Edge74,Edge78,Edge90,Edge94,Edge92,Edge131,Edge124,Edge129,Edge84,Edge126,Edge88,Edge117,Edge115,Edge70,Edge121,Edge119]
  BaseFeature = -> Chamfer
  Radius = 1
  SupportTransform = false
FEATURE [PartDesign::Fillet] Fillet003
  Base = -> Pocket014 [Edge1,Edge23,Edge37]
  BaseFeature = -> Pocket014
  Radius = 2
  SupportTransform = false
FEATURE [PartDesign::Fillet] Fillet004
  Base = -> Fillet003 [Edge28]
  BaseFeature = -> Fillet003
  Radius = 1.95
  SupportTransform = false
FEATURE [PartDesign::Chamfer] Chamfer001
  Angle = 45
  Base = -> Fillet004 [Edge10,Edge12,Edge11,Edge9]
  BaseFeature = -> Fillet004
  ChamferType = 0
  FlipDirection = false
  Size = 2
  Size2 = 1
  SupportTransform = false
FEATURE [PartDesign::Fillet] Fillet005
  Base = -> Chamfer001 [Edge8]
  BaseFeature = -> Chamfer001
  Radius = 1
  SupportTransform = false
FEATURE [Sketcher::SketchObject] Sketch038
  ExternalGeometry = -> [Pocket013]
  FullyConstrained = true
  MapMode = 5
  Placement = pos=(0,0,0) rot=(1,0,0;1.5708rad)
  Support = -> [Pocket013]
  constraints (1):
    c: DistanceX(g-3,g-3) = 14
FEATURE [Sketcher::SketchObject] Sketch039
  ExternalGeometry = -> [Pocket013]
  FullyConstrained = true
  MapMode = 5
  Placement = pos=(0,0,2) rot=(0,0,1;0rad)
  Support = -> [Pocket013]
  sketch-geometry (8):
    g0: LineSegment StartX=-22.4 StartY=5.5 StartZ=0 EndX=-11.6 EndY=5.5 EndZ=0
    g1: LineSegment StartX=-11.6 StartY=5.5 StartZ=0 EndX=-11.6 EndY=2 EndZ=0
    g2: LineSegment StartX=-11.6 StartY=2 StartZ=0 EndX=-22.4 EndY=2 EndZ=0
    g3: LineSegment StartX=-22.4 StartY=2 StartZ=0 EndX=-22.4 EndY=5.5 EndZ=0
    g4: LineSegment StartX=-11.6 StartY=33 StartZ=0 EndX=-17.6 EndY=33 EndZ=0
    g5: LineSegment StartX=-17.6 StartY=33 StartZ=0 EndX=-17.6 EndY=23 EndZ=0
    g6: LineSegment StartX=-17.6 StartY=23 StartZ=0 EndX=-11.6 EndY=23 EndZ=0
    g7: LineSegment StartX=-11.6 StartY=23 StartZ=0 EndX=-11.6 EndY=33 EndZ=0
  constraints (22):
    c: Coincident(g0,g1)
    c: Coincident(g1,g2)
    c: Coincident(g2,g3)
    c: Coincident(g3,g0)
    c: Horizontal(g0)
    c: Vertical(g1)
    c: Vertical(g3)
    c: Coincident(g4,g5)
    c: Coincident(g5,g6)
    c: Coincident(g6,g7)
    c: Coincident(g7,g4)
    c: Horizontal(g4)
    c: Horizontal(g6)
    c: Vertical(g5)
    c: Vertical(g7)
    c: Coincident(g2,g-4)
    c: Coincident(g1,g-5)
    c: Vertical(g6,g0)
    c: DistanceY(g-1,g6) = 23
    c: DistanceY(g5,g5) = 10
    c: DistanceX(g4,g4) = 6
    c: DistanceY(g1,g1) = 3.5
FEATURE [PartDesign::Pad] Pad016
  BaseFeature = -> Pocket013
  Direction = (1,1,1)
  Length = 16.5
  Length2 = 100
  Profile = -> Sketch039
  Type = 0
FEATURE [Sketcher::SketchObject] Sketch040
  ExternalGeometry = -> [Pad016]
  FullyConstrained = true
  MapMode = 5
  Placement = pos=(0,0,18.5) rot=(0,0,1;0rad)
  Support = -> [Pad016]
  sketch-geometry (2):
    g0: Circle CenterX=-14.5 CenterY=28 CenterZ=0 NormalX=0 NormalY=0 NormalZ=1 AngleXU=0 Radius=1
    g1: Circle CenterX=-17 CenterY=3.75 CenterZ=0 NormalX=0 NormalY=0 NormalZ=1 AngleXU=0 Radius=1
  constraints (6):
    c: Equal(g1,g0)
    c: Radius(g0) = 1
    c: DistanceX(g0,g-3) = 4.5
    c: DistanceX(g1,g-3) = 7
    c: DistanceY(g-3,g1) = 3.75
    c: DistanceY(g-3,g0) = 28
FEATURE [PartDesign::Pocket] Pocket018
  BaseFeature = -> Pad016
  Length = 10
  Length2 = 100
  Profile = -> Sketch040
  Type = 0
FEATURE [Sketcher::SketchObject] Sketch041
  FullyConstrained = true
  MapMode = 5
  Support = -> [XY_Plane003]
  sketch-geometry (4):
    g0: LineSegment StartX=-24 StartY=-58 StartZ=0 EndX=-10 EndY=-58 EndZ=0
    g1: LineSegment StartX=-10 StartY=-58 StartZ=0 EndX=-10 EndY=-10 EndZ=0
    g2: LineSegment StartX=-10 StartY=-10 StartZ=0 EndX=-24 EndY=-10 EndZ=0
    g3: LineSegment StartX=-24 StartY=-10 StartZ=0 EndX=-24 EndY=-58 EndZ=0
  constraints (12):
    c: Coincident(g0,g1)
    c: Coincident(g1,g2)
    c: Coincident(g2,g3)
    c: Coincident(g3,g0)
    c: Horizontal(g0)
    c: Horizontal(g2)
    c: Vertical(g1)
    c: Vertical(g3)
    c: DistanceY(g3,g3) = 48
    c: DistanceX(g2,g2) = 14
    c: DistanceX(g1,g-1) = 10
    c: DistanceY(g1,g-1) = 10
FEATURE [PartDesign::Pad] Pad017
  Direction = (1,1,1)
  Length = 2
  Length2 = 100
  Profile = -> Sketch041
  Type = 0
FEATURE [Sketcher::SketchObject] Sketch042
  ExternalGeometry = -> [Pocket018]
  FullyConstrained = true
  MapMode = 5
  Placement = pos=(0,0,20.5) rot=(0,0,1;0rad)
  Support = -> [Pocket018]
  constraints (9):
    c: DistanceX(g-11,g-4) = 1.6
    c: DistanceY(g-11,g-7) = 3.75
    c: DistanceY(g-11,g-4) = 2
    c: DistanceY(g-11,g-6) = 28
    c: DistanceX(g-6,g-11) = 4.5
    c: DistanceX(g-8,g-4) = 1.6
    c: DistanceY(g-4,g-8) = 8
    c: DistanceY(g-12,g-8) = 25
    c: DistanceX(g-7,g-11) = 7
FEATURE [Sketcher::SketchObject] Sketch043
  ExternalGeometry = -> [Pad017]
  FullyConstrained = true
  MapMode = 5
  Placement = pos=(0,0,0) rot=(1,0,0;3.14159rad)
  Support = -> [Pad017]
  sketch-geometry (8):
    g0: LineSegment StartX=-22.35 StartY=18.05 StartZ=0 EndX=-11.65 EndY=18.05 EndZ=0
    g1: LineSegment StartX=-11.65 StartY=18.05 StartZ=0 EndX=-11.65 EndY=35 EndZ=0
    g2: LineSegment StartX=-11.65 StartY=35 StartZ=0 EndX=-22.35 EndY=35 EndZ=0
    g3: LineSegment StartX=-22.35 StartY=35 StartZ=0 EndX=-22.35 EndY=18.05 EndZ=0
    g4: LineSegment StartX=-22.35 StartY=50.95 StartZ=0 EndX=-11.65 EndY=50.95 EndZ=0
    g5: LineSegment StartX=-11.65 StartY=50.95 StartZ=0 EndX=-11.65 EndY=55.95 EndZ=0
    g6: LineSegment StartX=-11.65 StartY=55.95 StartZ=0 EndX=-22.35 EndY=55.95 EndZ=0
    g7: LineSegment StartX=-22.35 StartY=55.95 StartZ=0 EndX=-22.35 EndY=50.95 EndZ=0
  constraints (24):
    c: Coincident(g0,g1)
    c: Coincident(g1,g2)
    c: Coincident(g2,g3)
    c: Coincident(g3,g0)
    c: Horizontal(g0)
    c: Horizontal(g2)
    c: Vertical(g1)
    c: Vertical(g3)
    c: Coincident(g4,g5)
    c: Coincident(g5,g6)
    c: Coincident(g6,g7)
    c: Coincident(g7,g4)
    c: Horizontal(g4)
    c: Horizontal(g6)
    c: Vertical(g5)
    c: Vertical(g7)
    c: DistanceX(g-4,g6) = 1.65
    c: DistanceX(g5,g-3) = 1.65
    c: DistanceY(g5,g-3) = 2.05
    c: DistanceY(g7,g7) = 5
    c: DistanceY(g-4,g0) = 8.05
    c: DistanceY(g-4,g2) = 25
    c: Vertical(g2,g4)
    c: Vertical(g4,g1)
FEATURE [PartDesign::Pad] Pad018
  BaseFeature = -> Pad017
  Direction = (1,1,1)
  Length = 2
  Length2 = 100
  Profile = -> Sketch043
  Type = 0
FEATURE [Sketcher::SketchObject] Sketch044
  ExternalGeometry = -> [Pad018]
  FullyConstrained = true
  MapMode = 5
  Placement = pos=(0,0,0) rot=(1,0,0;3.14159rad)
  Support = -> [Pad018]
  sketch-geometry (4):
    g0: LineSegment StartX=-22.35 StartY=12 StartZ=0 EndX=-11.65 EndY=12 EndZ=0
    g1: LineSegment StartX=-11.65 StartY=12 StartZ=0 EndX=-11.65 EndY=10 EndZ=0
    g2: LineSegment StartX=-11.65 StartY=10 StartZ=0 EndX=-22.35 EndY=10 EndZ=0
    g3: LineSegment StartX=-22.35 StartY=10 StartZ=0 EndX=-22.35 EndY=12 EndZ=0
  constraints (12):
    c: Coincident(g0,g1)
    c: Coincident(g1,g2)
    c: Coincident(g2,g3)
    c: Coincident(g3,g0)
    c: Horizontal(g0)
    c: Horizontal(g2)
    c: Vertical(g1)
    c: Vertical(g3)
    c: PointOnObject(g2,g-4)
    c: Vertical(g3,g-3)
    c: Vertical(g1,g-3)
    c: DistanceY(g3,g3) = 2
FEATURE [PartDesign::Pad] Pad019
  BaseFeature = -> Pad018
  Direction = (1,1,1)
  Length = 11
  Length2 = 100
  Profile = -> Sketch044
  Type = 0
FEATURE [Sketcher::SketchObject] Sketch045
  ExternalGeometry = -> [Pad019]
  FullyConstrained = true
  MapMode = 5
  Placement = pos=(0,0,2) rot=(0,0,1;0rad)
  Support = -> [Pad019]
  sketch-geometry (2):
    g0: Circle CenterX=-14.5 CenterY=-30 CenterZ=0 NormalX=0 NormalY=0 NormalZ=1 AngleXU=0 Radius=1.6
    g1: Circle CenterX=-17 CenterY=-54.25 CenterZ=0 NormalX=0 NormalY=0 NormalZ=1 AngleXU=0 Radius=1.6
  constraints (6):
    c: DistanceY(g-4,g0) = 28
    c: DistanceX(g0,g-4) = 4.5
    c: DistanceY(g-4,g1) = 3.75
    c: DistanceX(g1,g-4) = 7
    c: Equal(g0,g1)
    c: Radius(g0) = 1.6
FEATURE [PartDesign::Pocket] Pocket019
  BaseFeature = -> Pad019
  Length = 5
  Length2 = 100
  Profile = -> Sketch045
  Type = 0
FEATURE [PartDesign::Chamfer] Chamfer002
  Angle = 45
  Base = -> Pocket019 [Edge26,Edge25]
  BaseFeature = -> Pocket019
  ChamferType = 0
  FlipDirection = false
  Size = 1.5
  Size2 = 1
  SupportTransform = false
FEATURE [PartDesign::Fillet] Fillet006
  Base = -> Chamfer002 [Edge10,Edge9,Edge12,Edge14]
  BaseFeature = -> Chamfer002
  Radius = 1.5
  SupportTransform = false
FEATURE [PartDesign::Fillet] Fillet007
  Base = -> Fillet006 [Edge4]
  BaseFeature = -> Fillet006
  Radius = 1
  SupportTransform = false
FEATURE [PartDesign::Fillet] Fillet008
  Base = -> Fillet007 [Edge84,Edge85,Edge91,Edge93,Edge88,Edge86,Edge94,Edge92,Edge82,Edge83]
  BaseFeature = -> Fillet007
  Radius = 1
  SupportTransform = false
FEATURE [PartDesign::Body] Body003  label="sensor cap"
  Group = -> [Sketch041,Pad017,Sketch043,Pad018,Sketch044,Pad019,Sketch045,Pocket019,Chamfer002,Fillet006,Fillet007,Fillet008]
  Origin = -> Origin003
  Tip = -> Fillet008
FEATURE [PartDesign::Fillet] Fillet009
  Base = -> Pocket018 [Edge12,Edge13,Edge24,Edge26,Edge89,Edge94]
  BaseFeature = -> Pocket018
  Radius = 1.5
  SupportTransform = false
FEATURE [PartDesign::Fillet] Fillet010
  Base = -> Fillet009 [Edge73,Edge96]
  BaseFeature = -> Fillet009
  Radius = 1
  SupportTransform = false
FEATURE [PartDesign::Fillet] Fillet011
  Base = -> Fillet010 [Edge128]
  BaseFeature = -> Fillet010
  Radius = 1
  SupportTransform = false
FEATURE [PartDesign::Body] Body001  label="sensor body"
  Group = -> [Sketch020,Pad008,Sketch021,Pad009,Sketch022,Pad010,Sketch023,Pocket011,Sketch024,Pocket012,Sketch025,Pocket013,Sketch038,Sketch039,Pad016,Sketch040,Pocket018,Sketch042,Fillet009,Fillet010,Fillet011]
  Origin = -> Origin001
  Tip = -> Fillet011
FEATURE [Mesh::Feature] Mesh001  label="sensor body (Meshed)"
FEATURE [Mesh::Feature] Mesh003  label="sensor cap (Meshed)"
FEATURE [PartDesign::Chamfer] Chamfer003
  Angle = 45
  Base = -> Fillet005 [Edge145]
  BaseFeature = -> Fillet005
  ChamferType = 0
  FlipDirection = false
  Size = 1.2
  Size2 = 1
  SupportTransform = false
FEATURE [PartDesign::Chamfer] Chamfer004
  Angle = 45
  Base = -> Chamfer003 [Edge40]
  BaseFeature = -> Chamfer003
  ChamferType = 0
  FlipDirection = false
  Size = 1.2
  Size2 = 1
  SupportTransform = false
FEATURE [Sketcher::SketchObject] Sketch046
  ExternalGeometry = -> [Chamfer004]
  FullyConstrained = true
  MapMode = 5
  Placement = pos=(0,0,2) rot=(0,0,1;0rad)
  Support = -> [Chamfer004]
  constraints (4):
    c: DistanceY(g-7,g-3) = 4.7
    c: DistanceY(g-4,g-3) = 6.4
    c: DistanceY(g-5,g-3) = 8.4
    c: DistanceY(g-6,g-3) = 10.15
FEATURE [Sketcher::SketchObject] Sketch047
  ExternalGeometry = -> [Fillet002]
  FullyConstrained = true
  MapMode = 5
  Placement = pos=(0,0,-0.4) rot=(1,0,0;3.14159rad)
  Support = -> [Fillet002]
  sketch-geometry (8):
    g0: LineSegment StartX=3.1 StartY=21.3 StartZ=0 EndX=23.1 EndY=21.3 EndZ=0
    g1: LineSegment StartX=23.1 StartY=21.3 StartZ=0 EndX=23.1 EndY=20.15 EndZ=0
    g2: LineSegment StartX=23.1 StartY=20.15 StartZ=0 EndX=3.1 EndY=20.15 EndZ=0
    g3: LineSegment StartX=3.1 StartY=20.15 StartZ=0 EndX=3.1 EndY=21.3 EndZ=0
    g4: LineSegment StartX=3.1 StartY=18.4 StartZ=0 EndX=23.1 EndY=18.4 EndZ=0
    g5: LineSegment StartX=23.1 StartY=18.4 StartZ=0 EndX=23.1 EndY=17 EndZ=0
    g6: LineSegment StartX=23.1 StartY=17 StartZ=0 EndX=3.1 EndY=17 EndZ=0
    g7: LineSegment StartX=3.1 StartY=17 StartZ=0 EndX=3.1 EndY=18.4 EndZ=0
  constraints (22):
    c: Coincident(g0,g1)
    c: Coincident(g1,g2)
    c: Coincident(g2,g3)
    c: Coincident(g3,g0)
    c: Horizontal(g0)
    c: Horizontal(g2)
    c: Vertical(g1)
    c: Vertical(g3)
    c: DistanceY(g-3,g1) = 10.15
    c: Coincident(g0,g-6)
    c: DistanceX(g2,g2) = 20
    c: Coincident(g4,g5)
    c: Coincident(g5,g6)
    c: Coincident(g6,g7)
    c: Coincident(g7,g4)
    c: Horizontal(g4)
    c: Horizontal(g6)
    c: Vertical(g5)
    c: Vertical(g7)
    c: DistanceY(g-3,g4) = 8.4
    c: Coincident(g6,g-5)
    c: Vertical(g4,g1)
FEATURE [PartDesign::Pad] Pad020
  BaseFeature = -> Fillet002
  Direction = (1,1,1)
  Length = 2
  Length2 = 100
  Profile = -> Sketch047
  Type = 0
FEATURE [Sketcher::SketchObject] Sketch048
  ExternalGeometry = -> [Pad020]
  FullyConstrained = true
  MapMode = 5
  Placement = pos=(0,0,-1.2) rot=(1,0,0;3.14159rad)
  Support = -> [Pad020]
  sketch-geometry (8):
    g0: LineSegment StartX=3.1 StartY=14.7 StartZ=0 EndX=23.1 EndY=14.7 EndZ=0
    g1: LineSegment StartX=23.1 StartY=14.7 StartZ=0 EndX=23.1 EndY=12.1 EndZ=0
    g2: LineSegment StartX=23.1 StartY=12.1 StartZ=0 EndX=3.1 EndY=12.1 EndZ=0
    g3: LineSegment StartX=3.1 StartY=12.1 StartZ=0 EndX=3.1 EndY=14.7 EndZ=0
    g4: LineSegment StartX=3.1 StartY=17 StartZ=0 EndX=23.1 EndY=17 EndZ=0
    g5: LineSegment StartX=23.1 StartY=17 StartZ=0 EndX=23.1 EndY=16.4 EndZ=0
    g6: LineSegment StartX=23.1 StartY=16.4 StartZ=0 EndX=3.1 EndY=16.4 EndZ=0
    g7: LineSegment StartX=3.1 StartY=16.4 StartZ=0 EndX=3.1 EndY=17 EndZ=0
  constraints (22):
    c: Coincident(g0,g1)
    c: Coincident(g1,g2)
    c: Coincident(g2,g3)
    c: Coincident(g3,g0)
    c: Horizontal(g0)
    c: Horizontal(g2)
    c: Vertical(g1)
    c: Vertical(g3)
    c: Coincident(g2,g-4)
    c: Vertical(g-5,g0)
    c: Coincident(g4,g5)
    c: Coincident(g5,g6)
    c: Coincident(g6,g7)
    c: Coincident(g7,g4)
    c: Horizontal(g4)
    c: Horizontal(g6)
    c: Vertical(g5)
    c: Vertical(g7)
    c: Coincident(g4,g-5)
    c: Vertical(g5,g-5)
    c: DistanceY(g-3,g0) = 4.7
    c: DistanceY(g-3,g6) = 6.4
FEATURE [PartDesign::Pad] Pad021
  BaseFeature = -> Pad020
  Direction = (1,1,1)
  Length = 2
  Length2 = 100
  Profile = -> Sketch048
  Type = 0
FEATURE [PartDesign::Fillet] Fillet012
  Base = -> Pad021 [Edge213,Edge257,Edge264,Edge214,Edge259,Edge262,Edge242,Edge251,Edge247,Edge244,Edge191,Edge192]
  BaseFeature = -> Pad021
  Radius = 0.5
  SupportTransform = false
FEATURE [PartDesign::Chamfer] Chamfer005
  Angle = 45
  Base = -> Fillet012 [Edge91]
  BaseFeature = -> Fillet012
  ChamferType = 0
  FlipDirection = false
  Size = 0.5
  Size2 = 1
  SupportTransform = false
FEATURE [PartDesign::Chamfer] Chamfer006
  Angle = 45
  Base = -> Chamfer005 [Edge64,Edge87,Edge168]
  BaseFeature = -> Chamfer005
  ChamferType = 0
  FlipDirection = false
  Size = 0.5
  Size2 = 1
  SupportTransform = false
FEATURE [PartDesign::Fillet] Fillet013
  Base = -> Chamfer004 [Edge196,Edge295,Edge291,Edge203]
  BaseFeature = -> Chamfer004
  Radius = 1
  SupportTransform = false
FEATURE [PartDesign::Fillet] Fillet014
  Base = -> Fillet013 [Edge56,Edge300,Edge117,Edge363,Edge286,Edge307,Edge281,Edge362,Edge282,Edge155,Edge313,Edge312,Edge310,Edge309,Edge298,Edge283,Edge285,Edge284,Edge314,Edge267,Edge266]
  BaseFeature = -> Fillet013
  Radius = 0.9
  SupportTransform = false
FEATURE [Sketcher::SketchObject] Sketch049
  ExternalGeometry = -> [Fillet014]
  FullyConstrained = true
  MapMode = 5
  Placement = pos=(0,0,4.5) rot=(0,0,1;0rad)
  Support = -> [Fillet014]
  sketch-geometry (4):
    g0: LineSegment StartX=2 StartY=37.85 StartZ=0 EndX=5 EndY=37.85 EndZ=0
    g1: LineSegment StartX=5 StartY=37.85 StartZ=0 EndX=5 EndY=36.85 EndZ=0
    g2: LineSegment StartX=5 StartY=36.85 StartZ=0 EndX=2 EndY=36.85 EndZ=0
    g3: LineSegment StartX=2 StartY=36.85 StartZ=0 EndX=2 EndY=37.85 EndZ=0
  constraints (11):
    c: Coincident(g0,g1)
    c: Coincident(g1,g2)
    c: Coincident(g2,g3)
    c: Coincident(g3,g0)
    c: Horizontal(g0)
    c: Horizontal(g2)
    c: Vertical(g1)
    c: Vertical(g3)
    c: Coincident(g0,g-4)
    c: PointOnObject(g1,g-5)
    c: DistanceX(g0,g0) = 3
FEATURE [PartDesign::Pocket] Pocket020
  BaseFeature = -> Fillet014
  Length = 2.5
  Length2 = 100
  Profile = -> Sketch049
  Type = 0
FEATURE [Sketcher::SketchObject] Sketch050
  ExternalGeometry = -> [Pocket020]
  FullyConstrained = true
  MapMode = 5
  Placement = pos=(30,0,0) rot=(0.57735,-0.57735,-0.57735;2.0944rad)
  Support = -> [Pocket020]
  sketch-geometry (4):
    g0: LineSegment StartX=-46 StartY=14 StartZ=0 EndX=-41 EndY=14 EndZ=0
    g1: LineSegment StartX=-41 StartY=14 StartZ=0 EndX=-41 EndY=7 EndZ=0
    g2: LineSegment StartX=-41 StartY=7 StartZ=0 EndX=-46 EndY=7 EndZ=0
    g3: LineSegment StartX=-46 StartY=7 StartZ=0 EndX=-46 EndY=14 EndZ=0
  constraints (12):
    c: Coincident(g0,g1)
    c: Coincident(g1,g2)
    c: Coincident(g2,g3)
    c: Coincident(g3,g0)
    c: Horizontal(g0)
    c: Horizontal(g2)
    c: Vertical(g1)
    c: Vertical(g3)
    c: Vertical(g0,g-3)
    c: DistanceY(g0,g-3) = 5
    c: DistanceY(g-4,g2) = 5
    c: DistanceX(g0,g0) = 5
FEATURE [PartDesign::Pocket] Pocket021
  BaseFeature = -> Pocket020
  Length = 5
  Length2 = 100
  Profile = -> Sketch050
  Type = 0
FEATURE [PartDesign::Body] Body  label="main case"
  Group = -> [Sketch,Pad,Sketch001,Pad001,Sketch002,Pocket,Sketch003,Pad002,Sketch004,Pocket001,Sketch005,Pad003,Sketch006,Pad004,Sketch007,Pocket002,Sketch008,Pocket003,Sketch009,Pocket004,Sketch010,Pad005,Sketch011,Pad006,Sketch012,Pad007,Sketch013,Pocket005,Sketch014,Pocket006,Sketch015,Pocket007,Sketch016,Sketch017,Pocket008,Sketch018,Pocket009,Sketch019,Pocket010,Sketch026,Pocket014,Sketch029,Sketch030,+14 more]
  Origin = -> Origin
  Tip = -> Pocket021
FEATURE [Sketcher::SketchObject] Sketch051
  ExternalGeometry = -> [Chamfer006]
  FullyConstrained = true
  MapMode = 5
  Placement = pos=(0,0,-2.4) rot=(1,0,0;3.14159rad)
  Support = -> [Chamfer006]
  sketch-geometry (4):
    g0: LineSegment StartX=10.6 StartY=21.3 StartZ=0 EndX=16.6 EndY=21.3 EndZ=0
    g1: LineSegment StartX=16.6 StartY=21.3 StartZ=0 EndX=16.6 EndY=20.15 EndZ=0
    g2: LineSegment StartX=16.6 StartY=20.15 StartZ=0 EndX=10.6 EndY=20.15 EndZ=0
    g3: LineSegment StartX=10.6 StartY=20.15 StartZ=0 EndX=10.6 EndY=21.3 EndZ=0
  constraints (12):
    c: Coincident(g0,g1)
    c: Coincident(g1,g2)
    c: Coincident(g2,g3)
    c: Coincident(g3,g0)
    c: Horizontal(g0)
    c: Horizontal(g2)
    c: Vertical(g1)
    c: Vertical(g3)
    c: PointOnObject(g0,g-5)
    c: PointOnObject(g2,g-6)
    c: DistanceX(g-5,g0) = 7
    c: DistanceX(g0,g0) = 6
FEATURE [PartDesign::Pocket] Pocket022
  BaseFeature = -> Chamfer006
  Length = 2
  Length2 = 100
  Profile = -> Sketch051
  Type = 0
FEATURE [PartDesign::Fillet] Fillet015
  Base = -> Pocket022 [Edge157,Edge213,Edge153,Edge215]
  BaseFeature = -> Pocket022
  Radius = 0.5
  SupportTransform = false
FEATURE [PartDesign::Body] Body002  label="main cap"
  Group = -> [Sketch027,Pad011,Sketch028,Pad012,Sketch032,Pad013,Sketch033,Pad014,Sketch034,Pad015,Sketch035,Pocket015,Sketch036,Pocket016,Sketch037,Pocket017,Fillet,Fillet001,Chamfer,Fillet002,Sketch047,Pad020,Sketch048,Pad021,Fillet012,Chamfer005,Chamfer006,Sketch051,Pocket022,Fillet015]
  Origin = -> Origin002
  Tip = -> Fillet015
FEATURE [Mesh::Feature] Mesh  label="main case (Meshed)"
FEATURE [Mesh::Feature] Mesh004  label="main cap (Meshed)"
